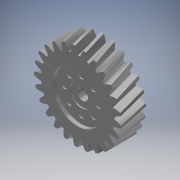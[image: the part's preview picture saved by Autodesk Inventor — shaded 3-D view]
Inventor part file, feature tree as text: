
AUTODESK INVENTOR PART (.ipt)
format: ipt  version: 2019 (Build 230136000, 136)  size: 582,144 bytes
history: native  units: mm (DEFAULTED — no unit token found)
features: sketch x10, extrude x7, plane x3, other x3, hole x2, chamfer x1
ambient origin geometry x8: Origin, YZ Plane, XZ Plane, XY Plane, X Axis, Y Axis, Z Axis, Center Point
bodies: Solid1 (feature_tree)
feature tree (26):
  extrude  "Extrusion1"  Depth=10.0mm TaperAngle=0.0deg
  plane  "Work Plane2"
  plane  "Work Plane8"
  plane  "Work Plane9"
  other  "Spur Gear"
  hole  "Hole1"  [1 undecoded]
  extrude  "Extrusion4"  Depth=1.256637mm TaperAngle=0.0deg
  extrude  "Extrusion6"  TaperAngle=0.0deg  [1 undecoded]
  hole  "Hole3"  [1 undecoded]
  extrude  "Extrusion8"  Depth=8.0mm
  chamfer  "Chamfer1"  Distance=1.5mm
  extrude  "Extrusion9"  Depth=9.0mm
  extrude  "Extrusion10"  Depth=5.0mm
  extrude  "Extrusion12"  Depth=5.0mm TaperAngle=0.0deg
  sketch  "Sketch1"  dims[d0=34.756617mm d1=10.0mm d2=0.0mm]
  sketch  "Sketch2"  dims[d3=32.258065mm d4=10.0mm d5=0.0mm]
  other  "Srf1"
  sketch  "Sketch5"  dims[d16=40.0mm d17=0.0mm d34=1.256637mm]
  sketch  "Sketch6"  dims[d39=0.0mm d41=0.0mm]
  sketch  "Sketch10"  dims[d43=40.0mm d46=40.0mm]
  sketch  "Sketch11"  dims[d47=0.0mm d48=0.0mm]
  sketch  "Sketch14"  dims[d55=4.5mm d56=6.0mm d57=6.5mm d58=4.0mm d59=90.0deg d60=8.0mm d61=20.594885mm d62=20.0mm d63=1.5mm d64=0.0mm]
  sketch  "Sketch15"  dims[d82=18.0mm d83=9.0mm]
  sketch  "Sketch16"  dims[d84=5.0mm d85=0.0mm d86=13.5mm]
  sketch  "Sketch18"  dims[d87=80.0mm d89=360.0deg d91=2.5mm d92=6.0mm d93=4.0mm d94=3.0mm d95=90.0deg d96=8.0mm d97=20.594885mm d100=5.0mm d101=0.0mm d102=1.5mm d103=4.0mm d104=12.217305mm d105=9.0mm d106=0.5mm d107=0.0mm d108=80.0mm d110=360.0deg d112=0.3mm d113=0.0mm d120=80.0mm d122=360.0deg d124=0.3mm d125=0.0mm]
  other  "Pitch Diameter"
note: 3 required parameter values undecoded (feature->parameter linkage not recoverable at this tier; creation-order binding heuristic only, values carry confidence <= 0.55)
